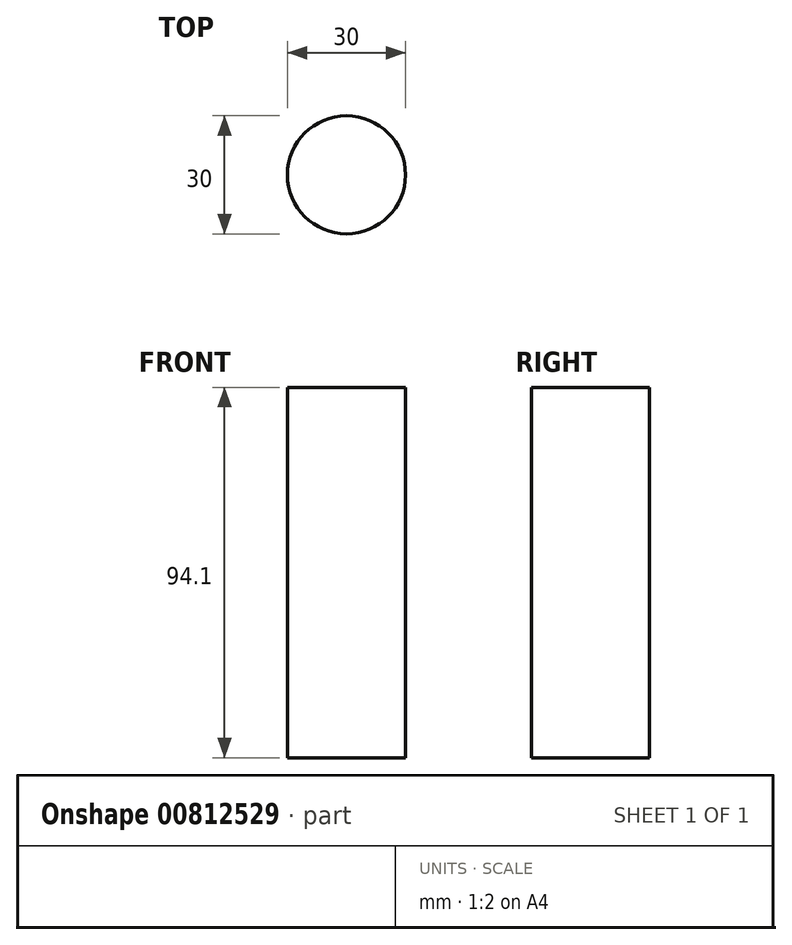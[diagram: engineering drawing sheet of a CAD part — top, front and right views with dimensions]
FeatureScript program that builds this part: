
annotation { "Feature Type Name" : "Feature", "Feature Type Description" : "" }
export const myFeature = defineFeature(function(context is Context, id is Id, definition is map)
    precondition{}
    {
        {
            var Q0;
            Q0=qCreatedBy(makeId("Top.planeOp"),FACE);
            var sketch = newSketch(context, id + "F0", { "sketchPlane" : qUnion([Q0])});
            skCircle(sketch, "E0", {"center": v(0, 0) * mm, "radius": 15 * mm});
            skSolve(sketch);
        }
        {
            var Q0;
            Q0=makeQuery(id+"F0.imprint","IMPRINT",FACE,{"disambiguationData":[TD([[makeQuery(id+"F0.imprint","IMPRINT",EDGE,{"derivedFrom":sQuery(id+"F0.wireOp",EDGE,"E0")}),1.0]])]});
            extrude(context, id + "F1", {"entities" : qUnion([Q0]), "depth" : 94.1 * mm, "offsetDistance" : 25 * mm});
        }
    });
